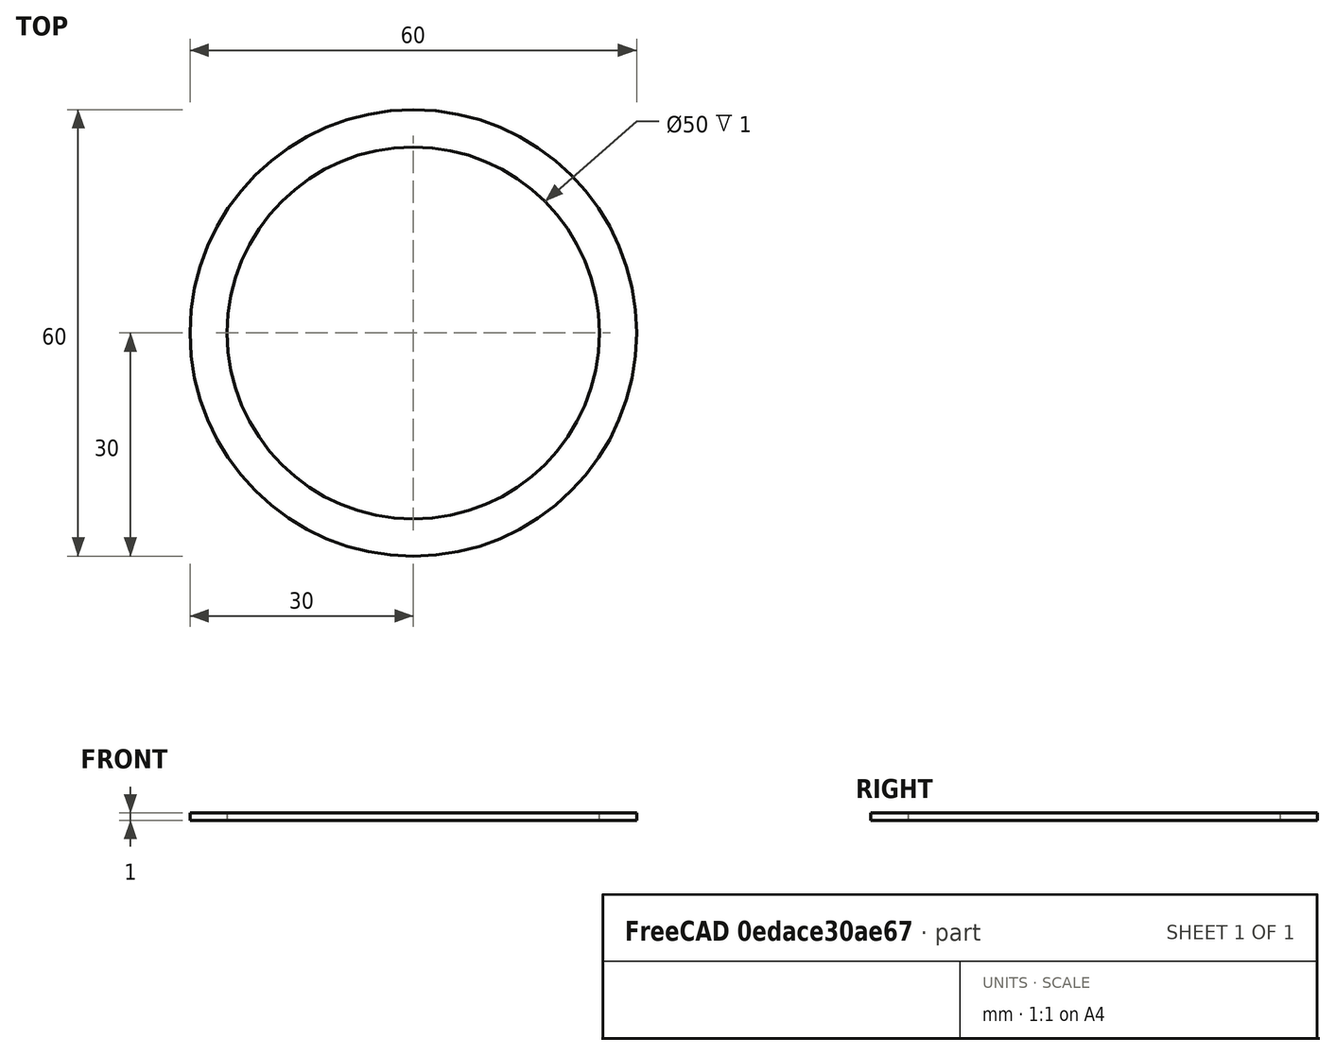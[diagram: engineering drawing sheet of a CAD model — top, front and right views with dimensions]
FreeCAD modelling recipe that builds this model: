
FCSTD DOCUMENT  (FreeCAD 0.19R24276 (Git))
Label: Bear_ring_fork_fork_down_d50_d60_h1
License: All rights reserved
LicenseURL: http://en.wikipedia.org/wiki/All_rights_reserved
objects: Sketcher::SketchObject×1, PartDesign::Pad×1, PartDesign::Body×1
note: 4 computed .brp shape members not serialized (recipe doc carries the construction recipe); baked Part::Feature solids carry a one-line shape summary decoded from their .brp

FEATURE [Sketcher::SketchObject] Sketch  label="Sketch_d50_d60"
  FullyConstrained = true
  MapMode = 5
  Support = -> [XY_Plane]
  sketch-geometry (2):
    g0: Circle CenterX=0 CenterY=0 CenterZ=0 NormalX=0 NormalY=0 NormalZ=1 AngleXU=0 Radius=25
    g1: Circle CenterX=0 CenterY=0 CenterZ=0 NormalX=0 NormalY=0 NormalZ=1 AngleXU=0 Radius=30
  constraints (4):
    c: Coincident(g0,g-1)
    c: Coincident(g1,g0)
    c: Diameter(g0) = 50
    c: Diameter(g1) = 60
FEATURE [PartDesign::Pad] Pad  label="Pad_h1"
  Direction = (1,1,1)
  Length = 1
  Length2 = 100
  Profile = -> Sketch
  Type = 0
FEATURE [PartDesign::Body] Body
  Group = -> [Sketch,Pad]
  Origin = -> Origin
  Tip = -> Pad
